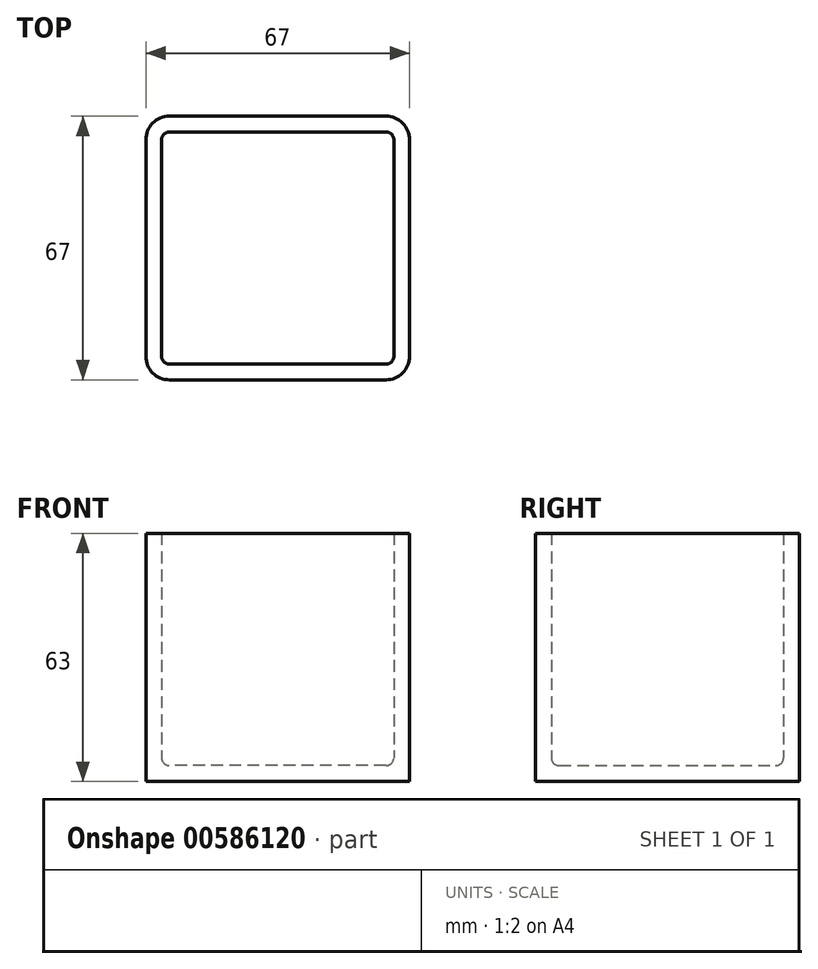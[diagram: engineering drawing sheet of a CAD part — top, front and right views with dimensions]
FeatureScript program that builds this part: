
annotation { "Feature Type Name" : "Feature", "Feature Type Description" : "" }
export const myFeature = defineFeature(function(context is Context, id is Id, definition is map)
    precondition{}
    {
        {
            var Q0;
            Q0=qCreatedBy(makeId("Top.planeOp"),FACE);
            var sketch = newSketch(context, id + "F0", { "sketchPlane" : qUnion([Q0])});
            skLineSegment(sketch, "E0.bottom", {"start": v(-29.5, 29.5) * mm, "end": v(29.5, 29.5) * mm});
            skLineSegment(sketch, "E0.top", {"start": v(-29.5, -29.5) * mm, "end": v(29.5, -29.5) * mm});
            skLineSegment(sketch, "E0.left", {"start": v(-29.5, 29.5) * mm, "end": v(-29.5, -29.5) * mm});
            skLineSegment(sketch, "E0.right", {"start": v(29.5, 29.5) * mm, "end": v(29.5, -29.5) * mm});
            skLineSegment(sketch, "E1.bottom", {"start": v(-33.5, 33.5) * mm, "end": v(33.5, 33.5) * mm});
            skLineSegment(sketch, "E1.top", {"start": v(-33.5, -33.5) * mm, "end": v(33.5, -33.5) * mm});
            skLineSegment(sketch, "E1.left", {"start": v(-33.5, 33.5) * mm, "end": v(-33.5, -33.5) * mm});
            skLineSegment(sketch, "E1.right", {"start": v(33.5, 33.5) * mm, "end": v(33.5, -33.5) * mm});
            skSolve(sketch);
        }
        {
            var Q0;
            Q0=makeQuery(id+"F0.imprint","IMPRINT",FACE,{"disambiguationData":[TD([[makeQuery(id+"F0.imprint","IMPRINT",EDGE,{"derivedFrom":sQuery(id+"F0.wireOp",EDGE,"E0.bottom")}),-1.0]])]});
            var Q1;
            Q1=makeQuery(id+"F0.imprint","IMPRINT",FACE,{"disambiguationData":[TD([[makeQuery(id+"F0.imprint","IMPRINT",EDGE,{"derivedFrom":sQuery(id+"F0.wireOp",EDGE,"E0.bottom")}),1.0]])]});
            extrude(context, id + "F1", {"entities" : qUnion([Q0, Q1]), "depth" : 4 * mm, "offsetDistance" : 25 * mm});
        }
        {
            var Q0;
            Q0=makeQuery(id+"F0.imprint","IMPRINT",FACE,{"disambiguationData":[TD([[makeQuery(id+"F0.imprint","IMPRINT",EDGE,{"derivedFrom":sQuery(id+"F0.wireOp",EDGE,"E0.bottom")}),1.0]])]});
            extrude(context, id + "F2", {"entities" : qUnion([Q0]), "operationType" : NewBodyOperationType.ADD, "depth" : 63 * mm, "offsetDistance" : 25 * mm});
        }
        {
            var Q0;
            Q0=makeQuery(id+"F2.opExtrude","SWEPT_EDGE",EDGE,{"disambiguationData":[OSD([sQuery(id+"F0.wireOp",EDGE,"E0.top"),sQuery(id+"F0.wireOp",EDGE,"E0.right")])]});
            var Q1;
            Q1=makeQuery(id+"F2.opExtrude","SWEPT_EDGE",EDGE,{"disambiguationData":[OSD([sQuery(id+"F0.wireOp",EDGE,"E0.top"),sQuery(id+"F0.wireOp",EDGE,"E0.left")])]});
            var Q2;
            Q2=makeQuery(id+"F2.opExtrude","SWEPT_EDGE",EDGE,{"disambiguationData":[OSD([sQuery(id+"F0.wireOp",EDGE,"E0.bottom"),sQuery(id+"F0.wireOp",EDGE,"E0.left")])]});
            var Q3;
            Q3=makeQuery(id+"F2.opExtrude","SWEPT_EDGE",EDGE,{"disambiguationData":[OSD([sQuery(id+"F0.wireOp",EDGE,"E0.bottom"),sQuery(id+"F0.wireOp",EDGE,"E0.right")])]});
            var Q4;
            Q4=makeQuery(id+"F2.boolean.opBoolean","INTERSECT",EDGE,{"derivedFrom":[makeQuery(id+"F1.opExtrude","CAP_FACE",FACE,{"disambiguationData":[OSD([sQuery(id+"F0.wireOp",EDGE,"E1.bottom"),sQuery(id+"F0.wireOp",EDGE,"E1.top"),sQuery(id+"F0.wireOp",EDGE,"E1.left"),sQuery(id+"F0.wireOp",EDGE,"E1.right")])],"isStart":false}),makeQuery(id+"F2.opExtrude","SWEPT_FACE",FACE,{"disambiguationData":[OSD([sQuery(id+"F0.wireOp",EDGE,"E0.left")])]})]});
            var Q5;
            Q5=makeQuery(id+"F2.boolean.opBoolean","INTERSECT",EDGE,{"derivedFrom":[makeQuery(id+"F1.opExtrude","CAP_FACE",FACE,{"disambiguationData":[OSD([sQuery(id+"F0.wireOp",EDGE,"E1.bottom"),sQuery(id+"F0.wireOp",EDGE,"E1.top"),sQuery(id+"F0.wireOp",EDGE,"E1.left"),sQuery(id+"F0.wireOp",EDGE,"E1.right")])],"isStart":false}),makeQuery(id+"F2.opExtrude","SWEPT_FACE",FACE,{"disambiguationData":[OSD([sQuery(id+"F0.wireOp",EDGE,"E0.bottom")])]})]});
            var Q6;
            Q6=makeQuery(id+"F2.boolean.opBoolean","INTERSECT",EDGE,{"derivedFrom":[makeQuery(id+"F1.opExtrude","CAP_FACE",FACE,{"disambiguationData":[OSD([sQuery(id+"F0.wireOp",EDGE,"E1.bottom"),sQuery(id+"F0.wireOp",EDGE,"E1.top"),sQuery(id+"F0.wireOp",EDGE,"E1.left"),sQuery(id+"F0.wireOp",EDGE,"E1.right")])],"isStart":false}),makeQuery(id+"F2.opExtrude","SWEPT_FACE",FACE,{"disambiguationData":[OSD([sQuery(id+"F0.wireOp",EDGE,"E0.right")])]})]});
            var Q7;
            Q7=makeQuery(id+"F2.boolean.opBoolean","INTERSECT",EDGE,{"derivedFrom":[makeQuery(id+"F1.opExtrude","CAP_FACE",FACE,{"disambiguationData":[OSD([sQuery(id+"F0.wireOp",EDGE,"E1.bottom"),sQuery(id+"F0.wireOp",EDGE,"E1.top"),sQuery(id+"F0.wireOp",EDGE,"E1.left"),sQuery(id+"F0.wireOp",EDGE,"E1.right")])],"isStart":false}),makeQuery(id+"F2.opExtrude","SWEPT_FACE",FACE,{"disambiguationData":[OSD([sQuery(id+"F0.wireOp",EDGE,"E0.top")])]})]});
            fillet(context, id + "F3", {"entities" : qUnion([Q0, Q1, Q2, Q3, Q4, Q5, Q6, Q7]), "radius" : 2 * mm, "tangentPropagation" : true, "allowEdgeOverflow" : false});
        }
        {
            var Q0;
            {var subQ0=sQuery(id+"F0.wireOp",EDGE,"E1.left");var subQ1=sQuery(id+"F0.wireOp",EDGE,"E1.bottom");Q0=makeQuery(id+"F2.boolean.opBoolean","MERGE",EDGE,{"derivedFrom":[makeQuery(id+"F1.opExtrude","SWEPT_EDGE",EDGE,{"disambiguationData":[OSD([subQ1,subQ0])]}),makeQuery(id+"F2.opExtrude","SWEPT_EDGE",EDGE,{"disambiguationData":[OSD([subQ1,subQ0])]})]});}
            var Q1;
            {var subQ0=sQuery(id+"F0.wireOp",EDGE,"E1.left");var subQ1=sQuery(id+"F0.wireOp",EDGE,"E1.top");Q1=makeQuery(id+"F2.boolean.opBoolean","MERGE",EDGE,{"derivedFrom":[makeQuery(id+"F1.opExtrude","SWEPT_EDGE",EDGE,{"disambiguationData":[OSD([subQ1,subQ0])]}),makeQuery(id+"F2.opExtrude","SWEPT_EDGE",EDGE,{"disambiguationData":[OSD([subQ1,subQ0])]})]});}
            var Q2;
            {var subQ0=sQuery(id+"F0.wireOp",EDGE,"E1.right");var subQ1=sQuery(id+"F0.wireOp",EDGE,"E1.top");Q2=makeQuery(id+"F2.boolean.opBoolean","MERGE",EDGE,{"derivedFrom":[makeQuery(id+"F1.opExtrude","SWEPT_EDGE",EDGE,{"disambiguationData":[OSD([subQ1,subQ0])]}),makeQuery(id+"F2.opExtrude","SWEPT_EDGE",EDGE,{"disambiguationData":[OSD([subQ1,subQ0])]})]});}
            var Q3;
            {var subQ0=sQuery(id+"F0.wireOp",EDGE,"E1.right");var subQ1=sQuery(id+"F0.wireOp",EDGE,"E1.bottom");Q3=makeQuery(id+"F2.boolean.opBoolean","MERGE",EDGE,{"derivedFrom":[makeQuery(id+"F1.opExtrude","SWEPT_EDGE",EDGE,{"disambiguationData":[OSD([subQ1,subQ0])]}),makeQuery(id+"F2.opExtrude","SWEPT_EDGE",EDGE,{"disambiguationData":[OSD([subQ1,subQ0])]})]});}
            fillet(context, id + "F4", {"entities" : qUnion([Q0, Q1, Q2, Q3]), "radius" : 6 * mm, "tangentPropagation" : true, "allowEdgeOverflow" : false});
        }
    });
